# Revit family: 20100-presto
name_source: partatom
category: Plumbing Fixtures
units: mm (PartAtom-declared; Revit-internal decimal feet)

## family parameters
Always vertical = Yes
Cut with Voids When Loaded = No
Maintain Annotation Orientation = No
OmniClass Number = 23.45.00.00
OmniClass Title = Sanitary, Laundry, and Cleaning Equipment
Part Type = Normal
Room Calculation Point = No
Round Connector Dimension = Use Diameter
Shared = No
Work Plane-Based = Yes

## types (1)
- 20100-presto
    - Hydraulic supply = 12.5 "
    -Delivered with = 1 G 1/2" nut for 12x14 tube with filter gasket
    > Standards & approvals = Acoustic class I
    > Thermal resistance : = 75.0000 (h·ft²·°F)/BTU
    Assembly Code = 20100
    Default Elevation = 1219 mm
    Description = Single wall-mounted tap2 position directional grid: 17° or 25
    Manufacturer = PRESTO
    Model = 20100
    URL = https://www.prestodatashare.com
    brand = LES ROBINETS PRESTO
    flow = 4 GPM
    power = 0 VA
    pressure = 5.00 psi
    ref = 20100 - PRESTOMAT 2010

## geometry (parser evidence)
native form markers: Sweep x2
no freeform markers — native parametric forms only
